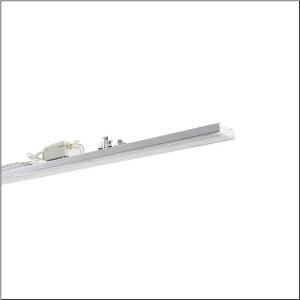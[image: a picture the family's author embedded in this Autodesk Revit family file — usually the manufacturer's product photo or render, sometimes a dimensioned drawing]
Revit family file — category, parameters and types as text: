
# Revit family: licross_r__11_recessed_ho_51te1ecn4cxs_7c7a
name_source: partatom
category: Lighting Fixtures
units: mm (PartAtom-declared; Revit-internal decimal feet)

## family parameters
Cut with Voids When Loaded = No
Host = Face
Light Source = No
Part Type = Normal
Room Calculation Point = No
Round Connector Dimension = Use Diameter
Shared = No

## types (1)
- --- (1 x LED, 12420 lm, 66.5 W, 4000K)
    Apparent Load = 67 VA
    CIE Flux Codes = 85 95 99 100 100
    Color Rendering = 80
    Color Temperature = 4000K
    Default Elevation = 1800 mm
    Description = Licross® 11 Recessed HO, luminaire insert, of sheet steel, galvanised, coil coated, white, length: 1.500mm, width: 66mm, height: 67mm, LED rated luminous flux: 12.420lm, light colour: 840, SDCM (Standard Deviation of Colour Matching)MacAdam ≤ 2 SDCM (initial), control gear: ON/OFF Multilumen, CLOi, with plug, 3-pole, with phase selection, mains connection: 220..240V, AC, 50/60Hz, start of lifetime: 67W, end of service life: 75W, internal wiring halogen-free, primary light control with lens, of plastic, primary optical cover: cover, of PMMA, light emission: direct distribution, primary light characteristic: symmetric, protection rating (complete): IP54, insulation class (complete): insulation class I (protective earthing), certification: CE, ENEC, VDE, UKCA, protection symbol: D if used in an environment with non-conductive dust loads with corresponding accessories, impact resistance: IK06, permissible ambient temperature for indoor applications: -35..+35°C, corresponds to IFS (International Featured Standards) requirements for safety and quality in the food industry, reducing of maximum allowable ambient temperature of 5°C with ceiling mounting, LABS conformity tested according to VDMA 24364:2018-05, packaging unit: 1 piece
    Height = 58 mm
    Lamp = 1 x LED
    Lamp Light Flux = 12420 lm
    Lamp Power = 66.5 W
    Lamp count = 1
    Length = 1500 mm
    Luminous efficacy = 187 lm/W
    Manufacturer = Siteco
    ModVariant = No
    Model = 51TE1ECN4CXS
    Mounting Place = Ceiling
    Mounting Type = Pendant
    Number of Poles = 1
    OnlyDefault = Yes
    Power Factor = 1
    Product Name = Licross® 11 Recessed HO
    Product group = luminaire insert | ceiling pendant
    ProductGroupID = 901
    Protection Class = Protection class I
    Protection Degree = IP 54
    RLX_Detail_Level = 1
    RLX_Emergency_Light_Flux = 0 lm
    RLX_Emergency_Type = 0
    RLX_Emergency_Type_DB = No
    RlxData = <blob elided: 22533 chars, md5=1313505e>
    Socket = socket
    Standby Power = 0 W
    System Light Flux = 12420 lm
    System Power = 67 W
    Type Comments = factory setting: luminous flux: 100 % | (A | C | E) | 156 mA
    Type Image = l_1296930.jpg
    URL = http://relux.com
    VarID = @adj_091933
    Voltage = 0 V
    Weight = 0.00 kg
    Width = 66 mm

## geometry (parser evidence)
native form markers: Blend x4, Sweep x12
no freeform markers — native parametric forms only
